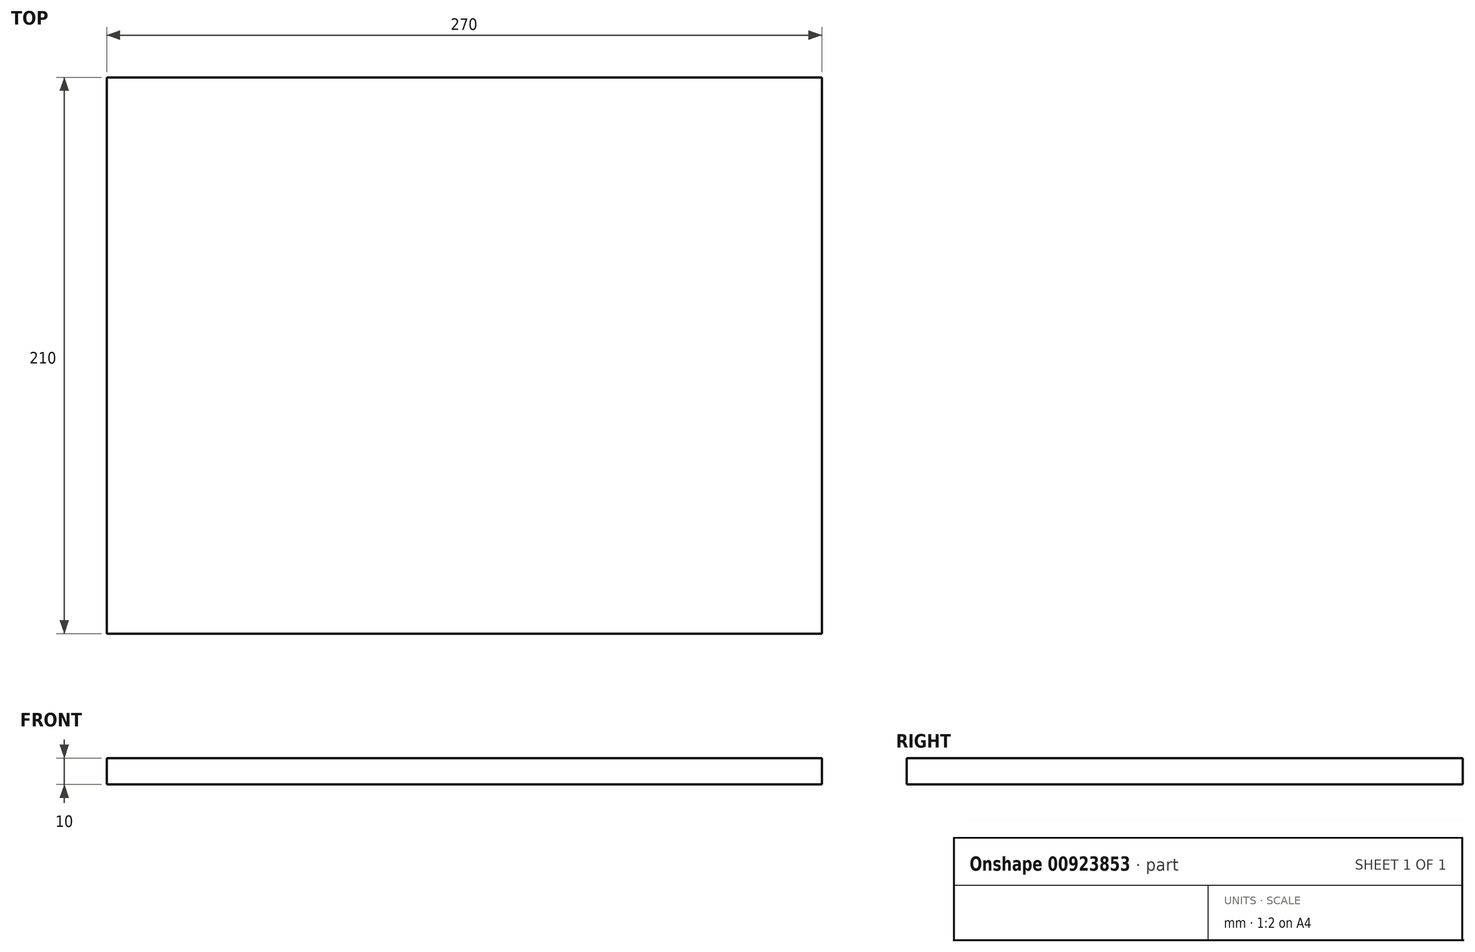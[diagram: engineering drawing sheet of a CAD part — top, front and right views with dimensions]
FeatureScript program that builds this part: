
annotation { "Feature Type Name" : "Feature", "Feature Type Description" : "" }
export const myFeature = defineFeature(function(context is Context, id is Id, definition is map)
    precondition{}
    {
        {
            var Q0;
            Q0=qCreatedBy(makeId("Top.planeOp"),FACE);
            var sketch = newSketch(context, id + "F0", { "sketchPlane" : qUnion([Q0])});
            skLineSegment(sketch, "E0.bottom", {"start": v(135, 105) * mm, "end": v(-135, 105) * mm});
            skLineSegment(sketch, "E0.top", {"start": v(135, -105) * mm, "end": v(-135, -105) * mm});
            skLineSegment(sketch, "E0.left", {"start": v(135, 105) * mm, "end": v(135, -105) * mm});
            skLineSegment(sketch, "E0.right", {"start": v(-135, 105) * mm, "end": v(-135, -105) * mm});
            skPoint(sketch, "E0.middle", {"position": v(0, 0) * mm});
            skPoint(sketch, "E1", {"position": v(-115, 0) * mm});
            skSolve(sketch);
        }
        {
            var Q0;
            Q0=makeQuery(id+"F0.imprint","IMPRINT",FACE,{"disambiguationData":[TD([[makeQuery(id+"F0.imprint","IMPRINT",EDGE,{"derivedFrom":sQuery(id+"F0.wireOp",EDGE,"E0.bottom")}),1.0]])]});
            var Q1;
            Q1=makeQuery(id+"F0.imprint","IMPRINT",FACE,{"disambiguationData":[TD([[makeQuery(id+"F0.imprint","IMPRINT",EDGE,{"derivedFrom":sQuery(id+"F0.wireOp",EDGE,"DOfoMCcq-8ObT-myeJ-42Uw-S4tERSy3AE3O.bottom")}),1.0]])]});
            extrude(context, id + "F1", {"entities" : qUnion([Q0, Q1]), "depth" : 10 * mm, "offsetDistance" : 25 * mm});
        }
    });
